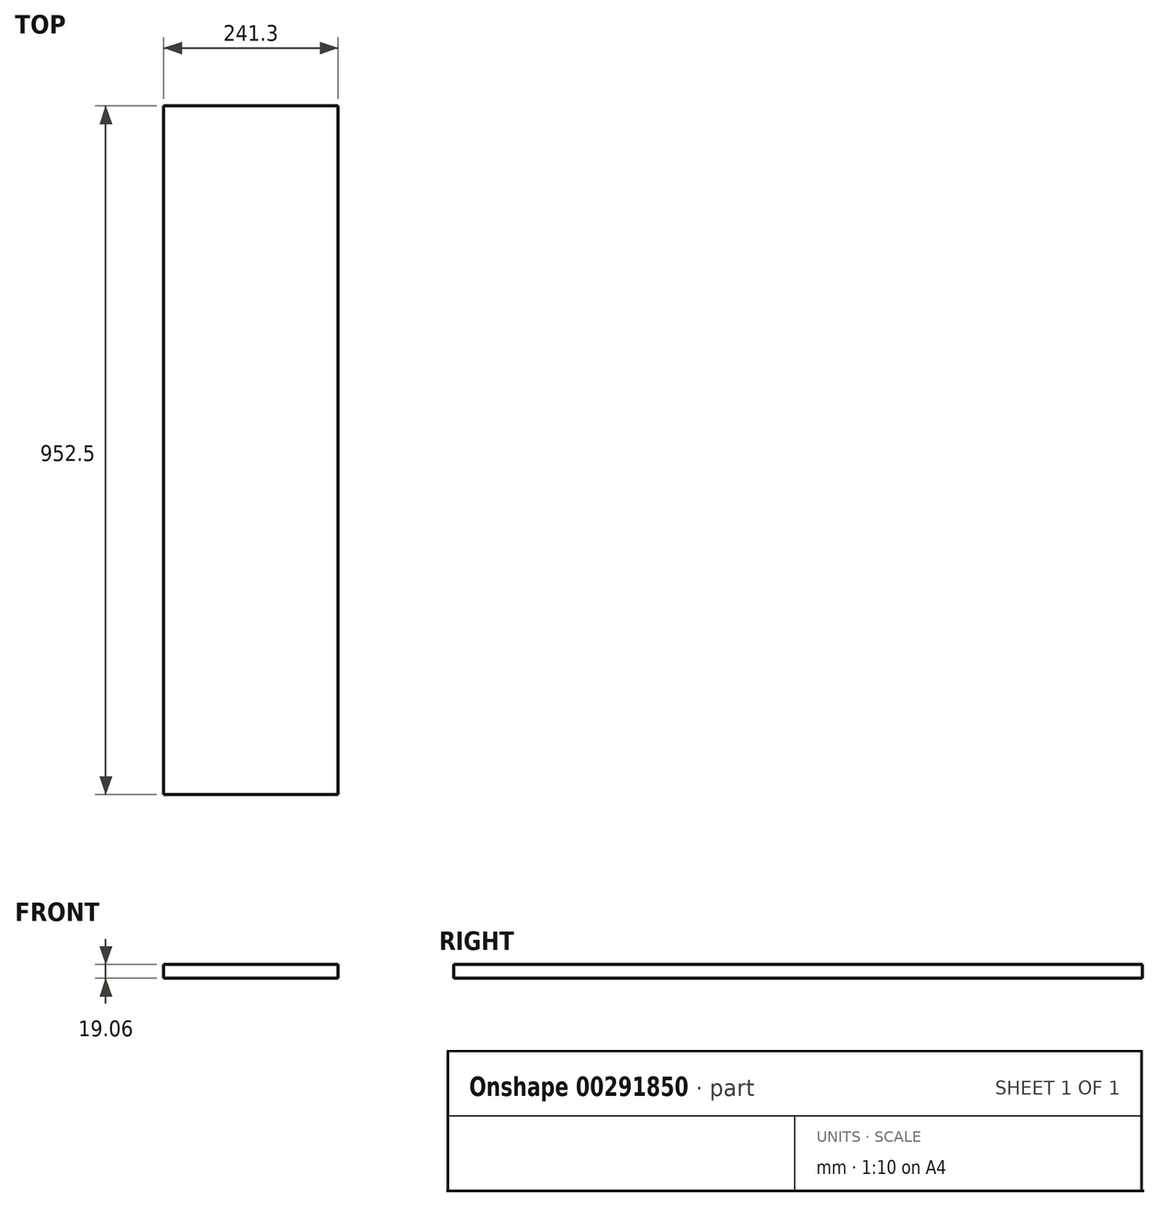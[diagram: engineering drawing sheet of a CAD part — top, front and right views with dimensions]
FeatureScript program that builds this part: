
annotation { "Feature Type Name" : "Feature", "Feature Type Description" : "" }
export const myFeature = defineFeature(function(context is Context, id is Id, definition is map)
    precondition{}
    {
        {
            var Q0;
            Q0=qCreatedBy(makeId("Front.planeOp"),FACE);
            var sketch = newSketch(context, id + "F0", { "sketchPlane" : qUnion([Q0])});
            skLineSegment(sketch, "E0.bottom", {"start": v(120.65, -9.53) * mm, "end": v(-120.65, -9.53) * mm});
            skLineSegment(sketch, "E0.top", {"start": v(120.65, 9.53) * mm, "end": v(-120.65, 9.53) * mm});
            skLineSegment(sketch, "E0.left", {"start": v(120.65, -9.53) * mm, "end": v(120.65, 9.53) * mm});
            skLineSegment(sketch, "E0.right", {"start": v(-120.65, -9.53) * mm, "end": v(-120.65, 9.52) * mm});
            skPoint(sketch, "E0.middle", {"position": v(0, 0) * mm});
            skSolve(sketch);
        }
        {
            var Q0;
            Q0 = qSketchRegion(id + "F0", true);
            extrude(context, id + "F1", {"entities" : qUnion([Q0]), "endBound" : BoundingType.SYMMETRIC, "depth" : 952.5 * mm});
        }
    });
